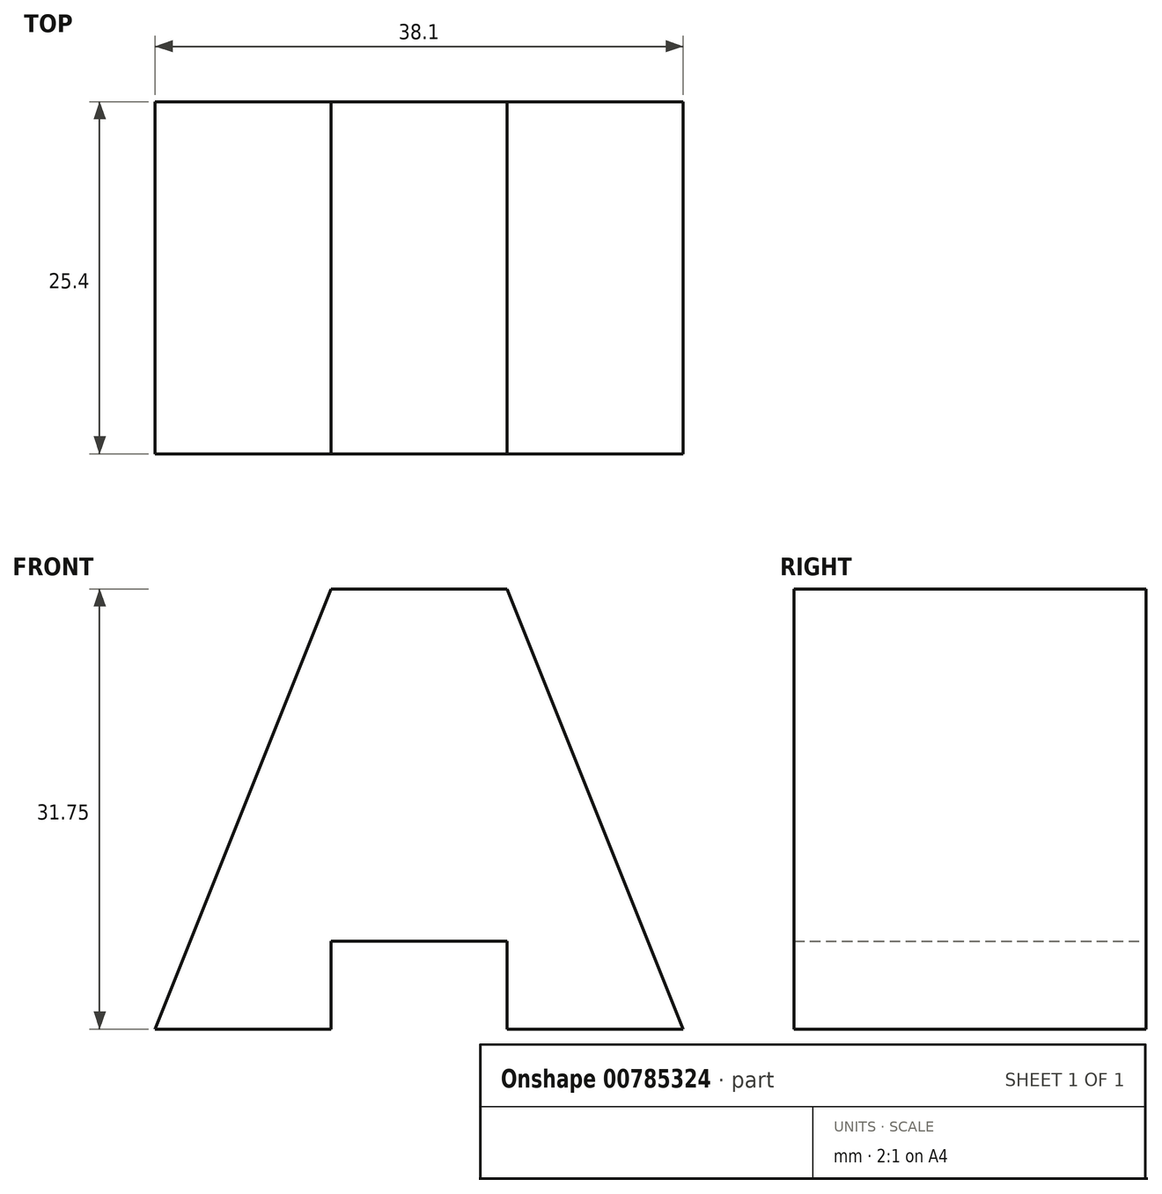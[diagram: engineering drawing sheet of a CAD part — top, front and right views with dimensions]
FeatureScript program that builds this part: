
annotation { "Feature Type Name" : "Feature", "Feature Type Description" : "" }
export const myFeature = defineFeature(function(context is Context, id is Id, definition is map)
    precondition{}
    {
        {
            var Q0;
            Q0=qCreatedBy(makeId("Front.planeOp"),FACE);
            var sketch = newSketch(context, id + "F0", { "sketchPlane" : qUnion([Q0])});
            skLineSegment(sketch, "E0", {"start": v(0, 0) * mm, "end": v(12.7, 0) * mm});
            skLineSegment(sketch, "E1", {"start": v(12.7, 0) * mm, "end": v(12.7, 6.35) * mm});
            skLineSegment(sketch, "E2", {"start": v(12.7, 6.35) * mm, "end": v(25.4, 6.35) * mm});
            skLineSegment(sketch, "E3", {"start": v(25.4, 6.35) * mm, "end": v(25.4, 0) * mm});
            skLineSegment(sketch, "E4", {"start": v(25.4, 0) * mm, "end": v(38.1, 0) * mm});
            skLineSegment(sketch, "E5", {"start": v(38.1, 0) * mm, "end": v(25.4, 31.75) * mm});
            skLineSegment(sketch, "E6", {"start": v(25.4, 31.75) * mm, "end": v(12.7, 31.75) * mm});
            skLineSegment(sketch, "E7", {"start": v(0, 0) * mm, "end": v(12.7, 31.75) * mm});
            skSolve(sketch);
        }
        {
            var Q0;
            Q0=makeQuery(id+"F0.imprint","IMPRINT",FACE,{"disambiguationData":[TD([[makeQuery(id+"F0.imprint","IMPRINT",EDGE,{"derivedFrom":sQuery(id+"F0.wireOp",EDGE,"E0")}),1.0]])]});
            extrude(context, id + "F1", {"entities" : qUnion([Q0]), "depth" : 25.4 * mm, "offsetDistance" : 25.4 * mm});
        }
    });
